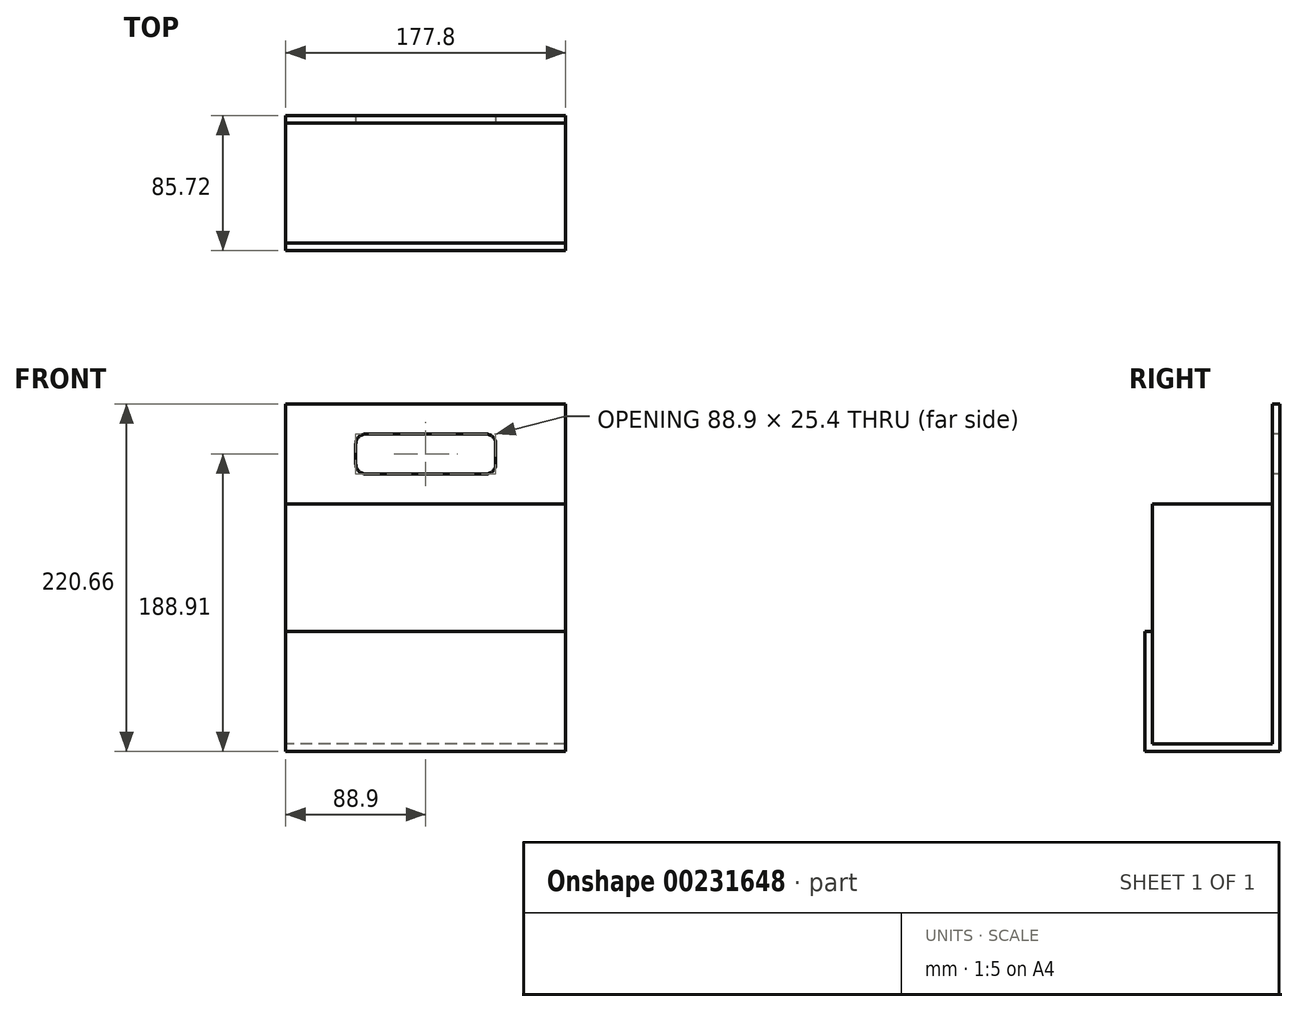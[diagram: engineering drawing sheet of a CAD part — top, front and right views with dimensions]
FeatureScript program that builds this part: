
annotation { "Feature Type Name" : "Feature", "Feature Type Description" : "" }
export const myFeature = defineFeature(function(context is Context, id is Id, definition is map)
    precondition{}
    {
        {
            var Q0;
            Q0=qCreatedBy(makeId("Right.planeOp"),FACE);
            var sketch = newSketch(context, id + "F0", { "sketchPlane" : qUnion([Q0])});
            skLineSegment(sketch, "E0.bottom", {"start": v(0, 0) * mm, "end": v(76.2, 0) * mm});
            skLineSegment(sketch, "E0.top", {"start": v(0, 152.4) * mm, "end": v(76.2, 152.4) * mm});
            skLineSegment(sketch, "E0.left", {"start": v(0, 0) * mm, "end": v(0, 152.4) * mm});
            skLineSegment(sketch, "E0.right", {"start": v(76.2, 0) * mm, "end": v(76.2, 152.4) * mm});
            skLineSegment(sketch, "E1", {"start": v(0, 71.44) * mm, "end": v(-4.76, 71.44) * mm});
            skLineSegment(sketch, "E2", {"start": v(-4.76, 71.44) * mm, "end": v(-4.76, -4.76) * mm});
            skLineSegment(sketch, "E3", {"start": v(-4.76, -4.76) * mm, "end": v(80.96, -4.76) * mm});
            skLineSegment(sketch, "E4", {"start": v(80.96, -4.76) * mm, "end": v(80.96, 215.9) * mm});
            skLineSegment(sketch, "E5", {"start": v(80.96, 215.9) * mm, "end": v(76.2, 215.9) * mm});
            skLineSegment(sketch, "E6", {"start": v(76.2, 215.9) * mm, "end": v(76.2, 152.4) * mm});
            skSolve(sketch);
        }
        {
            var Q0;
            {var subQ3=sQuery(id+"F0.wireOp",EDGE,"E0.bottom");Q0=makeQuery(id+"F0.imprint","IMPRINT",FACE,{"disambiguationData":[TD([[makeQuery(id+"F0.imprint","IMPRINT",EDGE,{"derivedFrom":subQ3}),1.0]])]});}
            extrude(context, id + "F1", {"entities" : qUnion([Q0]), "depth" : 88.9 * mm, "hasSecondDirection" : true, "secondDirectionOppositeDirection" : true, "secondDirectionDepth" : 88.9 * mm});
        }
        {
            var Q0;
            {var subQ2=sQuery(id+"F0.wireOp",EDGE,"E0.bottom");Q0=makeQuery(id+"F0.imprint","IMPRINT",FACE,{"disambiguationData":[TD([[makeQuery(id+"F0.imprint","IMPRINT",EDGE,{"derivedFrom":subQ2}),-1.0]])]});}
            extrude(context, id + "F2", {"entities" : qUnion([Q0]), "depth" : 88.9 * mm, "hasSecondDirection" : true, "secondDirectionOppositeDirection" : true, "secondDirectionDepth" : 88.9 * mm});
        }
        {
            var Q0;
            Q0=makeQuery(id+"F2.opExtrude","SWEPT_FACE",FACE,{"disambiguationData":[OSD([sQuery(id+"F0.wireOp",EDGE,"E0.right"),sQuery(id+"F0.wireOp",EDGE,"E6")])]});
            var sketch = newSketch(context, id + "F3", { "sketchPlane" : qUnion([Q0])});
            skLineSegment(sketch, "E7.bottom", {"start": v(38.1, 196.85) * mm, "end": v(-38.1, 196.85) * mm});
            skLineSegment(sketch, "E7.top", {"start": v(38.1, 171.45) * mm, "end": v(-38.1, 171.45) * mm});
            skLineSegment(sketch, "E7.left", {"start": v(44.45, 190.5) * mm, "end": v(44.45, 177.8) * mm});
            skLineSegment(sketch, "E7.right", {"start": v(-44.45, 190.5) * mm, "end": v(-44.45, 177.8) * mm});
            skPoint(sketch, "E7.middle", {"position": v(0, 184.15) * mm});
            skPoint(sketch, "E8", {"position": v(0, 215.9) * mm});
            skPoint(sketch, "E9.visualSharp", {"position": v(-44.45, 196.85) * mm});
            skArc(sketch, "E9.filletArc", {"start": v(-38.1, 196.85) * mm, "mid": v(-42.6, 195) * mm, "end": v(-44.45, 190.5) * mm});
            skPoint(sketch, "E10.visualSharp", {"position": v(-44.45, 171.45) * mm});
            skArc(sketch, "E10.filletArc", {"start": v(-44.45, 177.8) * mm, "mid": v(-42.6, 173.3) * mm, "end": v(-38.1, 171.45) * mm});
            skPoint(sketch, "E11.visualSharp", {"position": v(44.45, 171.45) * mm});
            skArc(sketch, "E11.filletArc", {"start": v(38.1, 171.45) * mm, "mid": v(42.6, 173.3) * mm, "end": v(44.45, 177.8) * mm});
            skPoint(sketch, "E12.visualSharp", {"position": v(44.45, 196.85) * mm});
            skArc(sketch, "E12.filletArc", {"start": v(44.45, 190.5) * mm, "mid": v(42.6, 195) * mm, "end": v(38.1, 196.85) * mm});
            skSolve(sketch);
        }
        {
            var Q0;
            Q0=makeQuery(id+"F3.imprint","IMPRINT",FACE,{"disambiguationData":[TD([[makeQuery(id+"F3.imprint","IMPRINT",EDGE,{"derivedFrom":sQuery(id+"F3.wireOp",EDGE,"E7.bottom")}),1.0]])]});
            extrude(context, id + "F4", {"entities" : qUnion([Q0]), "operationType" : NewBodyOperationType.REMOVE, "oppositeDirection" : true, "depth" : 25.4 * mm});
        }
    });
